# Revit family: Interseptor_Grease-Zurn-Z1173 01
name_source: partatom
category: Plumbing Fixtures
units: mm (PartAtom-declared; Revit-internal decimal feet)

## family parameters
Always vertical = Yes
Cut with Voids When Loaded = No
Maintain Annotation Orientation = No
OmniClass Number = 23.45.55.17
OmniClass Title = Mixing Faucets
Part Type = Normal
Room Calculation Point = No
Round Connector Dimension = Use Radius
Shared = No
Work Plane-Based = No

## types (16) — shared parameters
Assembly Code = D2090300
CW Connection = No
Default Elevation = 20 "
Description = EJECTO-MATIC GREASEPTOR
HW Connection = No
Manufacturer = Zurn Water, LLC
Manufacurer Brand = Zurn
Modified Date = 12/30/2025
Product Documentation Link = https://files.zurn.com
Product Page URL = https://www.zurn.com
Product data url = https://www.bimobject.com
URL = www.zurn.com
Vent Connection = No
WFU = 1
Waste Connection = Yes
zero-valued in all types: CWFU, HWFU

## per-type parameters (varying)
| type | "C" Dimension | "D" & "E" Dimension | "F" Dimension | "G" Dimension | "M" Dimension | Approx. Weight (Lbs) | Connector Radius | Flow Rate (GPM) | Grease Capacity | Main Material | Model | Pipe Size_A Inside Diameter | Pipe Size_A Inside Radius | Pipe Size_A Nominal Diameter | Pipe Size_A Outer Diameter | Pipe Size_A Outer Radius | Type Comments | Water Capacity |
| Z1173-200-7-2 | 11.25 " | 8.125 " | 21.75 " | 11.875 " | 6.125 " | 56 " | 1 " | 7 GPM | 14.00 lbf | Steel - Zurn - A.R.E Coated | Z1173 | 2.067 " | 1.034 " | 2 " | 2.375 " | 1.188 " | Z1173-200 With 2 Inch Inlet/Outlet (7 GPM) | 5.0 gal |
| Z1173-300-10-2 | 11.75 " | 8.25 " | 25.125 " | 14 " | 5.75 " | 70 " | 1 " | 10 GPM | 20.00 lbf | Steel - Zurn - A.R.E Coated | Z1173 | 2.067 " | 1.034 " | 2 " | 2.375 " | 1.188 " | Z1173-300 With 2 Inch Inlet/Outlet (10 GPM) | 6.0 gal |
| Z1173-400-15-3 | 13.375 " | 9.375 " | 27.125 " | 16.75 " | 6.875 " | 87 " | 1.5 " | 15 GPM | 30.00 lbf | Steel - Zurn - A.R.E Coated | Z1173 | 3.068 " | 1.534 " | 3 " | 3.5 " | 1.75 " | Z1173-400 With 3 Inch Inlet/Outlet (15 GPM) | 10.0 gal |
| Z1173-500-20-3 | 15 " | 11.75 " | 30 " | 17.25 " | 9.25 " | 104 " | 1.5 " | 20 GPM | 40.00 lbf | Steel - Zurn - A.R.E Coated | Z1173 | 3.068 " | 1.534 " | 3 " | 3.5 " | 1.75 " | Z1173-500 With 3 Inch Inlet/Outlet (20 GPM) | 16.0 gal |
| Z1173-600-25-3 | 17 " | 12.5 " | 32.25 " | 19.875 " | 9.5 " | 129 " | 1.5 " | 25 GPM | 50.00 lbf | Steel - Zurn - A.R.E Coated | Z1173 | 3.026 " | 1.513 " | 3 " | 3.5 " | 1.75 " | Z1173-600 With 3 Inch Inlet/Outlet (25 GPM) | 21.0 gal |
| Z1173-700-35-3 | 18.75 " | 14.5 " | 34.125 " | 22.5 " | 11.25 " | 156 " | 1.5 " | 35 GPM | 70.00 lbf | Steel - Zurn - A.R.E Coated | Z1173 | 3.026 " | 1.513 " | 3 " | 3.5 " | 1.75 " | Z1173-700 With 3 Inch Inlet/Outlet (35 GPM) | 30.0 gal |
| Z1173-800-50-3 | 21.5 " | 16 " | 36 " | 24.5 " | 13 " | 186 " | 1.5 " | 50 GPM | 100.00 lbf | Steel - Zurn - A.R.E Coated | Z1173 | 3.026 " | 1.513 " | 3 " | 3.5 " | 1.75 " | Z1173-800 With 3 Inch Inlet/Outlet (50 GPM) | 40.0 gal |
| Z1173-900-75-3 | 22.75 " | 18.5 " | 36 " | 28.625 " | 15.5 " | 316 " | 1.5 " | 75 GPM | 150.00 lbf | Steel - Zurn - A.R.E Coated | Z1173 | 3.026 " | 1.513 " | 3 " | 3.5 " | 1.75 " | Z1173-900 With 3 Inch Inlet/Outlet (75 GPM) | 65.0 gal |
| ZS1173-200-7-2 | 11.25 " | 8.125 " | 21.75 " | 11.875 " | 6.125 " | 56 " | 1 " | 7 GPM | 14.00 lbf | Steel - Zurn - Stainless - Type - 304 | ZS1173 | 2.067 " | 1.034 " | 2 " | 2.375 " | 1.188 " | ZS1173-200 With 2 Inch Inlet/Outlet (7 GPM) | 5.0 gal |
| ZS1173-300-10-2 | 11.75 " | 8.25 " | 25.125 " | 14 " | 5.75 " | 70 " | 1 " | 10 GPM | 20.00 lbf | Steel - Zurn - Stainless - Type - 304 | ZS1173 | 2.067 " | 1.034 " | 2 " | 2.375 " | 1.188 " | ZS1173-300 With 2 Inch Inlet/Outlet (10 GPM) | 6.0 gal |
| ZS1173-400-15-3 | 13.375 " | 9.375 " | 27.125 " | 16.75 " | 6.875 " | 87 " | 1.5 " | 15 GPM | 30.00 lbf | Steel - Zurn - Stainless - Type - 304 | ZS1173 | 3.068 " | 1.534 " | 3 " | 3.5 " | 1.75 " | ZS1173-400 With 3 Inch Inlet/Outlet (15 GPM) | 10.0 gal |
| ZS1173-500-20-3 | 15 " | 11.75 " | 30 " | 17.25 " | 9.25 " | 104 " | 1.5 " | 20 GPM | 40.00 lbf | Steel - Zurn - Stainless - Type - 304 | ZS1173 | 3.068 " | 1.534 " | 3 " | 3.5 " | 1.75 " | ZS1173-500 With 3 Inch Inlet/Outlet (20 GPM) | 16.0 gal |
| ZS1173-600-25-3 | 17 " | 12.5 " | 32.25 " | 19.875 " | 9.5 " | 129 " | 1.5 " | 25 GPM | 50.00 lbf | Steel - Zurn - Stainless - Type - 304 | ZS1173 | 3.026 " | 1.513 " | 3 " | 3.5 " | 1.75 " | ZS1173-600 With 3 Inch Inlet/Outlet (25 GPM) | 21.0 gal |
| ZS1173-700-35-3 | 18.75 " | 14.5 " | 34.125 " | 22.5 " | 11.25 " | 156 " | 1.5 " | 35 GPM | 70.00 lbf | Steel - Zurn - Stainless - Type - 304 | ZS1173 | 3.026 " | 1.513 " | 3 " | 3.5 " | 1.75 " | ZS1173-700 With 3 Inch Inlet/Outlet (35 GPM) | 30.0 gal |
| ZS1173-800-50-3 | 21.5 " | 16 " | 36 " | 24.5 " | 13 " | 186 " | 1.5 " | 50 GPM | 100.00 lbf | Steel - Zurn - Stainless - Type - 304 | ZS1173 | 3.026 " | 1.513 " | 3 " | 3.5 " | 1.75 " | ZS1173-800 With 3 Inch Inlet/Outlet (50 GPM) | 40.0 gal |
| ZS1173-900-75-3 | 22.75 " | 18.5 " | 36 " | 28.625 " | 15.5 " | 316 " | 1.5 " | 75 GPM | 150.00 lbf | Steel - Zurn - Stainless - Type - 304 | ZS1173 | 3.026 " | 1.513 " | 3 " | 3.5 " | 1.75 " | ZS1173-900 With 3 Inch Inlet/Outlet (75 GPM) | 65.0 gal |

## geometry (parser evidence)
native form markers: Blend x6, Sweep x2
no freeform markers — native parametric forms only
